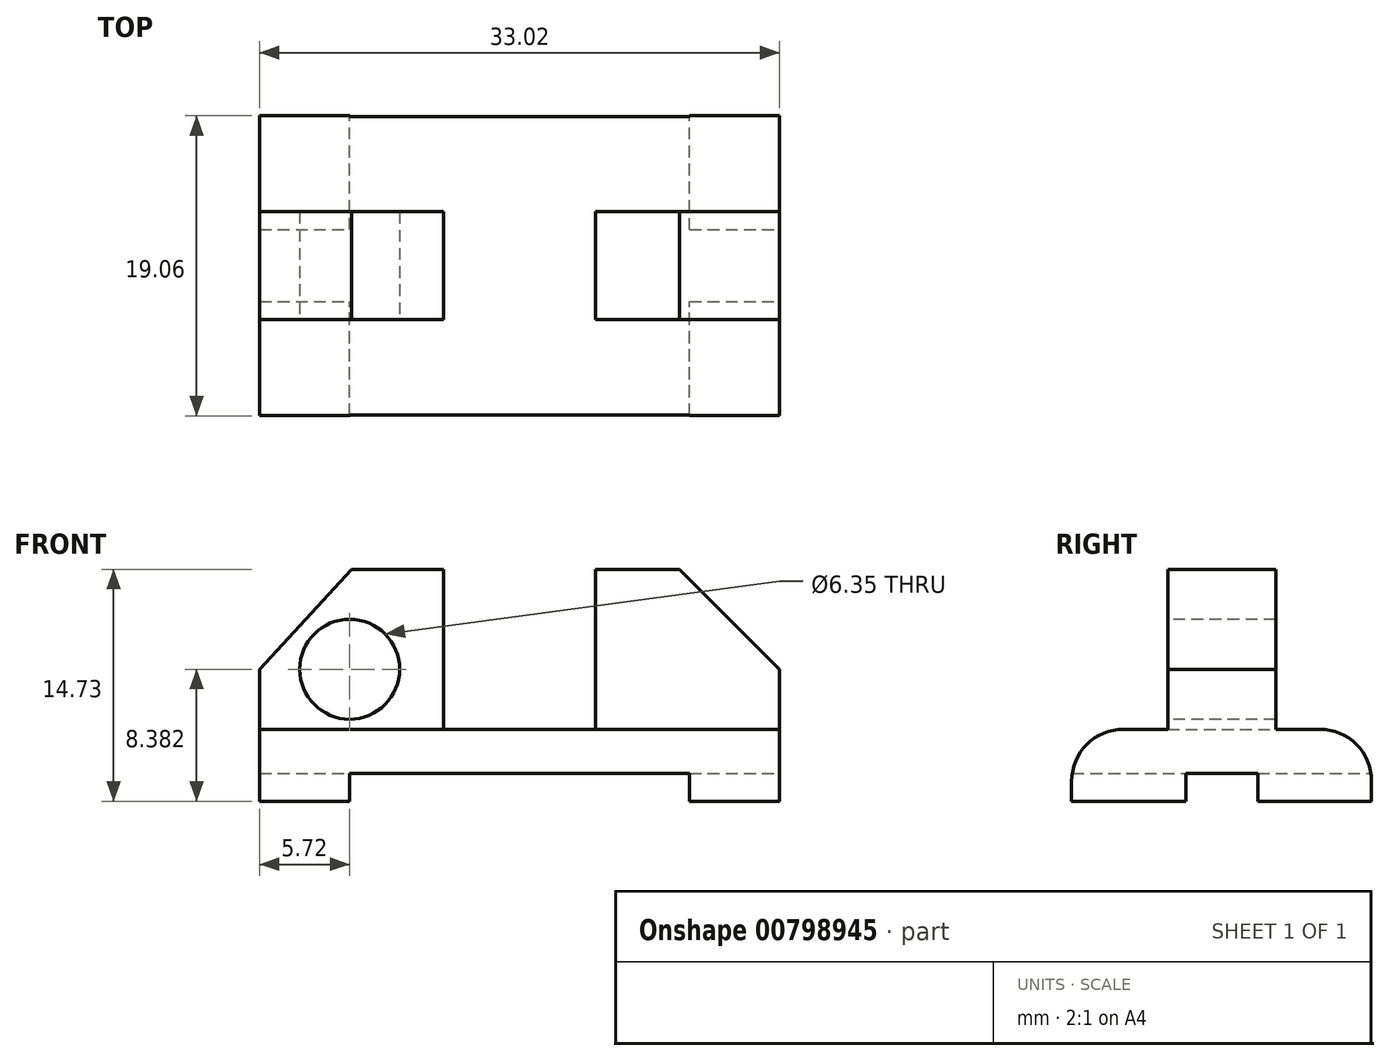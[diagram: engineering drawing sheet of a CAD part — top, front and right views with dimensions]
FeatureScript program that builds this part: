
annotation { "Feature Type Name" : "Feature", "Feature Type Description" : "" }
export const myFeature = defineFeature(function(context is Context, id is Id, definition is map)
    precondition{}
    {
        {
            var Q0;
            Q0=qCreatedBy(makeId("Front.planeOp"),FACE);
            var sketch = newSketch(context, id + "F0", { "sketchPlane" : qUnion([Q0])});
            skLineSegment(sketch, "E0", {"start": v(0, 0) * mm, "end": v(-5.72, 0) * mm});
            skLineSegment(sketch, "E1", {"start": v(-5.72, 0) * mm, "end": v(-5.72, 4.57) * mm});
            skLineSegment(sketch, "E2", {"start": v(-5.72, 4.57) * mm, "end": v(27.3, 4.57) * mm});
            skLineSegment(sketch, "E3", {"start": v(27.3, 4.57) * mm, "end": v(27.3, 0) * mm});
            skLineSegment(sketch, "E4", {"start": v(27.3, 0) * mm, "end": v(21.6, 0) * mm});
            skLineSegment(sketch, "E5", {"start": v(21.6, 0) * mm, "end": v(21.6, 1.78) * mm});
            skLineSegment(sketch, "E6", {"start": v(21.6, 1.78) * mm, "end": v(0, 1.78) * mm});
            skLineSegment(sketch, "E7", {"start": v(0, 1.78) * mm, "end": v(0, 0) * mm});
            skSolve(sketch);
        }
        {
            var Q0;
            Q0=makeQuery(id+"F0.imprint","IMPRINT",FACE,{"disambiguationData":[TD([[makeQuery(id+"F0.imprint","IMPRINT",EDGE,{"derivedFrom":sQuery(id+"F0.wireOp",EDGE,"E0")}),-1.0]])]});
            extrude(context, id + "F1", {"entities" : qUnion([Q0]), "endBound" : BoundingType.SYMMETRIC, "depth" : 19.05 * mm, "offsetDistance" : 25.4 * mm});
        }
        {
            var Q0;
            Q0=makeQuery(id+"F1.opExtrude","SWEPT_FACE",FACE,{"disambiguationData":[OSD([sQuery(id+"F0.wireOp",EDGE,"E3")])]});
            var sketch = newSketch(context, id + "F2", { "sketchPlane" : qUnion([Q0])});
            skLineSegment(sketch, "E8.bottom", {"start": v(0, 0) * mm, "end": v(2.29, 0) * mm});
            skLineSegment(sketch, "E8.top", {"start": v(0, 1.78) * mm, "end": v(2.29, 1.78) * mm});
            skLineSegment(sketch, "E8.right", {"start": v(2.29, 0) * mm, "end": v(2.29, 1.78) * mm});
            skLineSegment(sketch, "E9", {"start": v(0, 1.78) * mm, "end": v(-2.29, 1.78) * mm});
            skLineSegment(sketch, "E10", {"start": v(-2.29, 1.78) * mm, "end": v(-2.29, 0) * mm});
            skLineSegment(sketch, "E11", {"start": v(-2.29, 0) * mm, "end": v(0, 0) * mm});
            skSolve(sketch);
        }
        {
            var Q0;
            Q0=makeQuery(id+"F2.imprint","IMPRINT",FACE,{"disambiguationData":[TD([[makeQuery(id+"F2.imprint","IMPRINT",EDGE,{"derivedFrom":sQuery(id+"F2.wireOp",EDGE,"E8.bottom")}),1.0]])]});
            extrude(context, id + "F3", {"entities" : qUnion([Q0]), "operationType" : NewBodyOperationType.REMOVE, "oppositeDirection" : true, "depth" : 33.02 * mm, "offsetDistance" : 25.4 * mm});
        }
        {
            var Q0;
            Q0=makeQuery(id+"F1.opExtrude","CAP_EDGE",EDGE,{"disambiguationData":[OSD([sQuery(id+"F0.wireOp",EDGE,"E2")])],"isStart":false});
            var Q1;
            Q1=makeQuery(id+"F1.opExtrude","CAP_EDGE",EDGE,{"disambiguationData":[OSD([sQuery(id+"F0.wireOp",EDGE,"E2")])],"isStart":true});
            fillet(context, id + "F4", {"entities" : qUnion([Q0, Q1]), "radius" : 3.3 * mm, "tangentPropagation" : true, "allowEdgeOverflow" : false});
        }
        {
            var Q0;
            Q0=makeQuery(id+"F1.opExtrude","SWEPT_FACE",FACE,{"disambiguationData":[OSD([sQuery(id+"F0.wireOp",EDGE,"E2")])]});
            var sketch = newSketch(context, id + "F5", { "sketchPlane" : qUnion([Q0])});
            skLineSegment(sketch, "E12", {"start": v(-5.72, 0) * mm, "end": v(-5.72, 3.43) * mm});
            skLineSegment(sketch, "E13", {"start": v(-5.72, 0) * mm, "end": v(-5.72, -3.43) * mm});
            skLineSegment(sketch, "E14", {"start": v(-5.72, 3.43) * mm, "end": v(5.97, 3.43) * mm});
            skLineSegment(sketch, "E15", {"start": v(5.97, 3.43) * mm, "end": v(5.97, -3.43) * mm});
            skLineSegment(sketch, "E16", {"start": v(5.97, -3.43) * mm, "end": v(-5.72, -3.43) * mm});
            skLineSegment(sketch, "E17", {"start": v(27.3, 0) * mm, "end": v(27.3, 3.43) * mm});
            skLineSegment(sketch, "E18", {"start": v(27.3, 0) * mm, "end": v(27.3, -3.43) * mm});
            skLineSegment(sketch, "E19", {"start": v(27.3, -3.43) * mm, "end": v(15.62, -3.43) * mm});
            skLineSegment(sketch, "E20", {"start": v(15.62, -3.43) * mm, "end": v(15.62, 3.43) * mm});
            skLineSegment(sketch, "E21", {"start": v(15.62, 3.43) * mm, "end": v(27.3, 3.43) * mm});
            skSolve(sketch);
        }
        {
            var Q0;
            Q0=makeQuery(id+"F5.imprint","IMPRINT",FACE,{"disambiguationData":[TD([[makeQuery(id+"F5.imprint","IMPRINT",EDGE,{"derivedFrom":sQuery(id+"F5.wireOp",EDGE,"E12")}),-1.0]])]});
            var Q1;
            Q1=makeQuery(id+"F5.imprint","IMPRINT",FACE,{"disambiguationData":[TD([[makeQuery(id+"F5.imprint","IMPRINT",EDGE,{"derivedFrom":sQuery(id+"F5.wireOp",EDGE,"E17")}),1.0]])]});
            extrude(context, id + "F6", {"entities" : qUnion([Q0, Q1]), "operationType" : NewBodyOperationType.ADD, "depth" : 10.16 * mm, "offsetDistance" : 25.4 * mm});
        }
        {
            var Q0;
            Q0=makeQuery(id+"F6.opExtrude","SWEPT_FACE",FACE,{"disambiguationData":[OSD([sQuery(id+"F5.wireOp",EDGE,"E16")])]});
            var sketch = newSketch(context, id + "F7", { "sketchPlane" : qUnion([Q0])});
            skLineSegment(sketch, "E22", {"start": v(-5.72, 4.57) * mm, "end": v(-5.72, 8.38) * mm});
            skCircle(sketch, "E23", {"center": v(0, 8.38) * mm, "radius": 3.18 * mm});
            skLineSegment(sketch, "E24", {"start": v(-5.72, 8.38) * mm, "end": v(0.13, 14.73) * mm});
            skLineSegment(sketch, "E25", {"start": v(0.13, 14.73) * mm, "end": v(5.97, 14.73) * mm});
            skSolve(sketch);
        }
        {
            var Q0;
            {var subQ0=sQuery(id+"F7.wireOp",EDGE,"E24");Q0=makeQuery(id+"F7.imprint","IMPRINT",FACE,{"disambiguationData":[TD([[makeQuery(id+"F7.imprint","IMPRINT",EDGE,{"derivedFrom":subQ0}),1.0]])]});}
            var Q1;
            Q1=makeQuery(id+"F7.imprint","IMPRINT",FACE,{"disambiguationData":[TD([[makeQuery(id+"F7.imprint","IMPRINT",EDGE,{"derivedFrom":sQuery(id+"F7.wireOp",EDGE,"E23")}),1.0]])]});
            extrude(context, id + "F8", {"entities" : qUnion([Q0, Q1]), "operationType" : NewBodyOperationType.REMOVE, "oppositeDirection" : true, "depth" : 25.4 * mm, "offsetDistance" : 25.4 * mm});
        }
        {
            var Q0;
            Q0=makeQuery(id+"F6.opExtrude","SWEPT_FACE",FACE,{"disambiguationData":[OSD([sQuery(id+"F5.wireOp",EDGE,"E19")])]});
            var sketch = newSketch(context, id + "F9", { "sketchPlane" : qUnion([Q0])});
            skLineSegment(sketch, "E26", {"start": v(15.62, 14.73) * mm, "end": v(20.96, 14.73) * mm});
            skLineSegment(sketch, "E27", {"start": v(27.3, 4.57) * mm, "end": v(27.3, 8.38) * mm});
            skLineSegment(sketch, "E28", {"start": v(20.96, 14.73) * mm, "end": v(27.3, 8.38) * mm});
            skSolve(sketch);
        }
        {
            var Q0;
            {var subQ0=sQuery(id+"F9.wireOp",EDGE,"E28");Q0=makeQuery(id+"F9.imprint","IMPRINT",FACE,{"disambiguationData":[TD([[makeQuery(id+"F9.imprint","IMPRINT",EDGE,{"derivedFrom":subQ0}),1.0]])]});}
            extrude(context, id + "F10", {"entities" : qUnion([Q0]), "operationType" : NewBodyOperationType.REMOVE, "oppositeDirection" : true, "depth" : 25.4 * mm, "offsetDistance" : 25.4 * mm});
        }
    });
